# Revit family: 201_ROL __180-3+ROL-S
name_source: partatom
category: Air Terminals
units: mm (PartAtom-declared; Revit-internal decimal feet)

## family parameters
Always vertical = Yes
Cut with Voids When Loaded = No
Part Type = Normal
Room Calculation Point = Yes
Round Connector Dimension = Use Diameter
Shared = No
Work Plane-Based = No

## types (4) — shared parameters
CAT0 = Yes
CL_Location_5000 = 5000 mm  [stored 16.4042 ft]
Description = Supply air duct with damper/attenuator unit
L = 4500 mm  [stored 14.7638 ft]
LS1 = 1504 mm  [stored 4.93438 ft]
LS1__ve = -1504 mm  [stored -4.93438 ft]
L_ARR = 400 mm  [stored 1.31234 ft]
Manufacturer = Climecon
QmdConnectorList = 201;D
URL = www.climecon.fi
W_ARR = 400 mm  [stored 1.31234 ft]
X1 = 1450 mm  [stored 4.75722 ft]
XRefLineVPlnId = 7453
YRefLineVPlnId = 7456
magiPartTypeId = 201
magiProductFamilyId = ROL */180-3+ROL-S
zero-valued in all types: CLBTZ, H_ARR, MC_Default_elevation

## per-type parameters (varying)
| type | D | R |
| ROL 160/180-3+ROL-S | 160 mm | 83 mm |
| ROL 315/180-3+ROL-S | 315 mm | 160 mm  [stored 0.524934 ft] |
| ROL 250/180-3+ROL-S | 250 mm | 128 mm |
| ROL 200/180-3+ROL-S | 200 mm | 103 mm |

note: column(s) folded — value = type name in every type: magiProductCode, magiProductId

note: [stored X ft] marks values corroborated as IEEE doubles in the binary element streams (Revit-internal decimal feet)

## geometry (parser evidence)
native form markers: Sweep x2
no freeform markers — native parametric forms only
